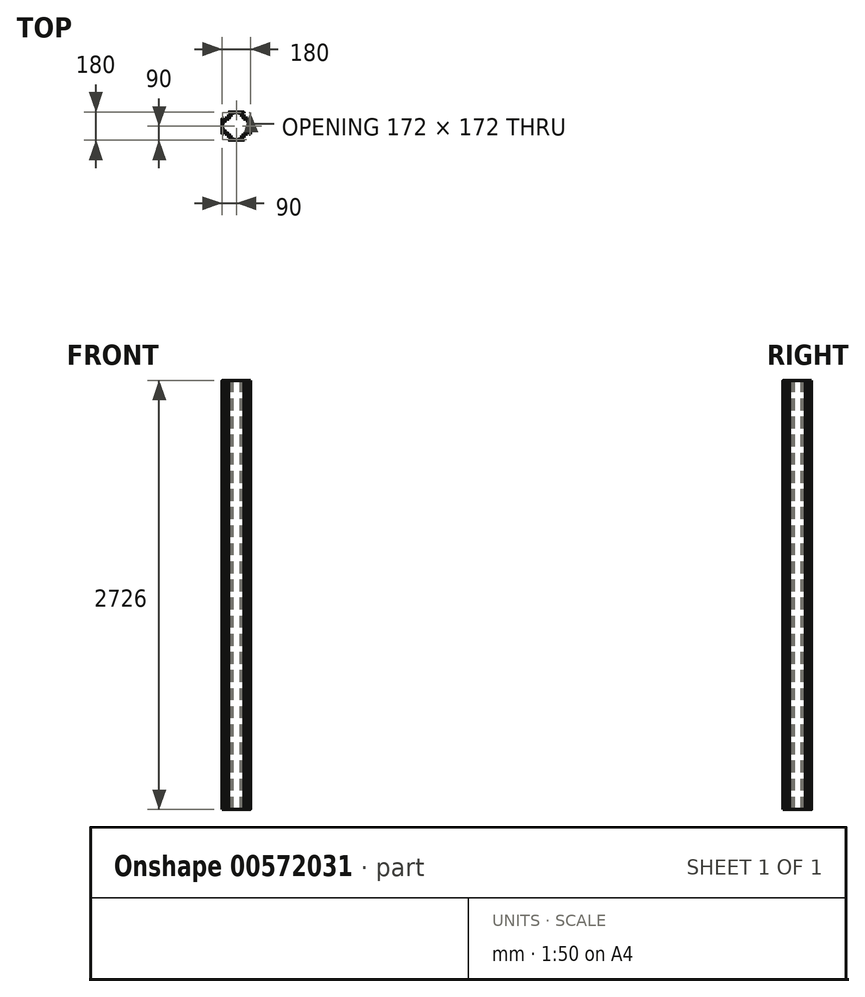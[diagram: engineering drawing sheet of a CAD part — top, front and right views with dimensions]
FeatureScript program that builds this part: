
annotation { "Feature Type Name" : "Feature", "Feature Type Description" : "" }
export const myFeature = defineFeature(function(context is Context, id is Id, definition is map)
    precondition{}
    {
        {
            var Q0;
            Q0=qCreatedBy(makeId("Top.planeOp"),FACE);
            var sketch = newSketch(context, id + "F0", { "sketchPlane" : qUnion([Q0])});
            skLineSegment(sketch, "E0", {"start": v(-58.4, 0) * mm, "end": v(68.52, 0) * mm, "construction": true});
            skLineSegment(sketch, "E1", {"start": v(0, 55.81) * mm, "end": v(0, -52.18) * mm, "construction": true});
            skLineSegment(sketch, "E2.bottom", {"start": v(-50, 90) * mm, "end": v(50, 90) * mm});
            skLineSegment(sketch, "E2.top", {"start": v(-50, -90) * mm, "end": v(50, -90) * mm});
            skLineSegment(sketch, "E2.left", {"start": v(-90, 50) * mm, "end": v(-90, -50) * mm});
            skLineSegment(sketch, "E2.right", {"start": v(90, 50) * mm, "end": v(90, -50) * mm});
            skLineSegment(sketch, "E3", {"start": v(-90, 50) * mm, "end": v(-82, 50) * mm});
            skLineSegment(sketch, "E4", {"start": v(-50, 50) * mm, "end": v(-50, 72) * mm});
            skLineSegment(sketch, "E5.MirrorCS", {"start": v(90, 50) * mm, "end": v(82, 50) * mm});
            skLineSegment(sketch, "E6.MirrorCS", {"start": v(50, 50) * mm, "end": v(50, 72) * mm});
            skLineSegment(sketch, "E7.MirrorCS", {"start": v(50, -50) * mm, "end": v(50, -72) * mm});
            skLineSegment(sketch, "E8.MirrorCS", {"start": v(90, -50) * mm, "end": v(82, -50) * mm});
            skLineSegment(sketch, "E9.MirrorCS", {"start": v(-50, -50) * mm, "end": v(-50, -72) * mm});
            skLineSegment(sketch, "E10.MirrorCS", {"start": v(-90, -50) * mm, "end": v(-82, -50) * mm});
            skLineSegment(sketch, "E11", {"start": v(-82, -50) * mm, "end": v(-82, -46) * mm});
            skLineSegment(sketch, "E12", {"start": v(-82, -46) * mm, "end": v(-86, -46) * mm});
            skLineSegment(sketch, "E13", {"start": v(-86, -46) * mm, "end": v(-86, -38) * mm});
            skLineSegment(sketch, "E14", {"start": v(-86, -38) * mm, "end": v(-68, -38) * mm});
            skLineSegment(sketch, "E15", {"start": v(-68, -38) * mm, "end": v(-68, -46) * mm});
            skLineSegment(sketch, "E16", {"start": v(-68, -46) * mm, "end": v(-72, -46) * mm});
            skLineSegment(sketch, "E17", {"start": v(-72, -46) * mm, "end": v(-72, -50) * mm});
            skLineSegment(sketch, "E18.MirrorCS", {"start": v(-68, 46) * mm, "end": v(-72, 46) * mm});
            skLineSegment(sketch, "E19.MirrorCS", {"start": v(-86, 38) * mm, "end": v(-68, 38) * mm});
            skLineSegment(sketch, "E20.MirrorCS", {"start": v(-82, 50) * mm, "end": v(-82, 46) * mm});
            skLineSegment(sketch, "E21.MirrorCS", {"start": v(-86, 46) * mm, "end": v(-86, 38) * mm});
            skLineSegment(sketch, "E22.MirrorCS", {"start": v(-82, 46) * mm, "end": v(-86, 46) * mm});
            skLineSegment(sketch, "E23.MirrorCS", {"start": v(-68, 38) * mm, "end": v(-68, 46) * mm});
            skLineSegment(sketch, "E24.MirrorCS", {"start": v(-72, 46) * mm, "end": v(-72, 50) * mm});
            skLineSegment(sketch, "E25.MirrorCS", {"start": v(68, -38) * mm, "end": v(68, -46) * mm});
            skLineSegment(sketch, "E26.MirrorCS", {"start": v(86, 38) * mm, "end": v(68, 38) * mm});
            skLineSegment(sketch, "E27.MirrorCS", {"start": v(82, 46) * mm, "end": v(86, 46) * mm});
            skLineSegment(sketch, "E28.MirrorCS", {"start": v(86, -38) * mm, "end": v(68, -38) * mm});
            skLineSegment(sketch, "E29.MirrorCS", {"start": v(68, 46) * mm, "end": v(72, 46) * mm});
            skLineSegment(sketch, "E30.MirrorCS", {"start": v(86, 46) * mm, "end": v(86, 38) * mm});
            skLineSegment(sketch, "E31.MirrorCS", {"start": v(86, -46) * mm, "end": v(86, -38) * mm});
            skLineSegment(sketch, "E32.MirrorCS", {"start": v(72, -46) * mm, "end": v(72, -50) * mm});
            skLineSegment(sketch, "E33.MirrorCS", {"start": v(82, 50) * mm, "end": v(82, 46) * mm});
            skLineSegment(sketch, "E34.MirrorCS", {"start": v(72, 46) * mm, "end": v(72, 50) * mm});
            skLineSegment(sketch, "E35.MirrorCS", {"start": v(68, 38) * mm, "end": v(68, 46) * mm});
            skLineSegment(sketch, "E36.MirrorCS", {"start": v(82, -50) * mm, "end": v(82, -46) * mm});
            skLineSegment(sketch, "E37.MirrorCS", {"start": v(68, -46) * mm, "end": v(72, -46) * mm});
            skLineSegment(sketch, "E38.MirrorCS", {"start": v(82, -46) * mm, "end": v(86, -46) * mm});
            skLineSegment(sketch, "E39", {"start": v(-50, 50) * mm, "end": v(0, 0) * mm, "construction": true});
            skLineSegment(sketch, "E40.MirrorCS", {"start": v(-38, 68) * mm, "end": v(-46, 68) * mm});
            skLineSegment(sketch, "E41.MirrorCS", {"start": v(-46, 68) * mm, "end": v(-46, 72) * mm});
            skLineSegment(sketch, "E42.MirrorCS", {"start": v(-46, 72) * mm, "end": v(-50, 72) * mm});
            skLineSegment(sketch, "E43.MirrorCS", {"start": v(-38, 86) * mm, "end": v(-38, 68) * mm});
            skLineSegment(sketch, "E44.MirrorCS", {"start": v(-46, 86) * mm, "end": v(-38, 86) * mm});
            skLineSegment(sketch, "E45.MirrorCS", {"start": v(-50, 82) * mm, "end": v(-46, 82) * mm});
            skLineSegment(sketch, "E46.MirrorCS", {"start": v(-46, 82) * mm, "end": v(-46, 86) * mm});
            skLineSegment(sketch, "E47.MirrorCS", {"start": v(46, 82) * mm, "end": v(46, 86) * mm});
            skLineSegment(sketch, "E48.MirrorCS", {"start": v(38, 86) * mm, "end": v(38, 68) * mm});
            skLineSegment(sketch, "E49.MirrorCS", {"start": v(46, 68) * mm, "end": v(46, 72) * mm});
            skLineSegment(sketch, "E50.MirrorCS", {"start": v(50, 82) * mm, "end": v(46, 82) * mm});
            skLineSegment(sketch, "E51.MirrorCS", {"start": v(46, 86) * mm, "end": v(38, 86) * mm});
            skLineSegment(sketch, "E52.MirrorCS", {"start": v(38, 68) * mm, "end": v(46, 68) * mm});
            skLineSegment(sketch, "E53.MirrorCS", {"start": v(46, 72) * mm, "end": v(50, 72) * mm});
            skLineSegment(sketch, "E54.MirrorCS", {"start": v(-46, -86) * mm, "end": v(-38, -86) * mm});
            skLineSegment(sketch, "E55.MirrorCS", {"start": v(50, -82) * mm, "end": v(46, -82) * mm});
            skLineSegment(sketch, "E56.MirrorCS", {"start": v(-38, -86) * mm, "end": v(-38, -68) * mm});
            skLineSegment(sketch, "E57.MirrorCS", {"start": v(-46, -82) * mm, "end": v(-46, -86) * mm});
            skLineSegment(sketch, "E58.MirrorCS", {"start": v(-38, -68) * mm, "end": v(-46, -68) * mm});
            skLineSegment(sketch, "E59.MirrorCS", {"start": v(38, -86) * mm, "end": v(38, -68) * mm});
            skLineSegment(sketch, "E60.MirrorCS", {"start": v(-50, -82) * mm, "end": v(-46, -82) * mm});
            skLineSegment(sketch, "E61.MirrorCS", {"start": v(-46, -72) * mm, "end": v(-50, -72) * mm});
            skLineSegment(sketch, "E62.MirrorCS", {"start": v(-46, -68) * mm, "end": v(-46, -72) * mm});
            skLineSegment(sketch, "E63.MirrorCS", {"start": v(46, -72) * mm, "end": v(50, -72) * mm});
            skLineSegment(sketch, "E64.MirrorCS", {"start": v(38, -68) * mm, "end": v(46, -68) * mm});
            skLineSegment(sketch, "E65.MirrorCS", {"start": v(46, -68) * mm, "end": v(46, -72) * mm});
            skLineSegment(sketch, "E66.MirrorCS", {"start": v(46, -82) * mm, "end": v(46, -86) * mm});
            skLineSegment(sketch, "E67.MirrorCS", {"start": v(46, -86) * mm, "end": v(38, -86) * mm});
            skLineSegment(sketch, "E68.trimOffspring", {"start": v(-72, 50) * mm, "end": v(-50, 50) * mm});
            skLineSegment(sketch, "E69.trimOffspring", {"start": v(-50, 82) * mm, "end": v(-50, 90) * mm});
            skLineSegment(sketch, "E70.trimOffspring", {"start": v(50, 82) * mm, "end": v(50, 90) * mm});
            skLineSegment(sketch, "E71.trimOffspring", {"start": v(72, 50) * mm, "end": v(50, 50) * mm});
            skLineSegment(sketch, "E72.trimOffspring", {"start": v(72, -50) * mm, "end": v(50, -50) * mm});
            skLineSegment(sketch, "E73.trimOffspring", {"start": v(50, -82) * mm, "end": v(50, -90) * mm});
            skLineSegment(sketch, "E74.trimOffspring", {"start": v(-50, -82) * mm, "end": v(-50, -90) * mm});
            skLineSegment(sketch, "E75.trimOffspring", {"start": v(-72, -50) * mm, "end": v(-50, -50) * mm});
            skSolve(sketch);
        }
        {
            var Q0;
            Q0=qSketchRegion(id+"F0",true);
            extrude(context, id + "F1", {"entities" : qUnion([Q0]), "depth" : 2726 * mm, "offsetDistance" : 25 * mm});
        }
        {
            var Q0;
            Q0=makeQuery(id+"F1.opExtrude","CAP_FACE",FACE,{"disambiguationData":[OSD([sQuery(id+"F0.wireOp",EDGE,"E2.bottom"),sQuery(id+"F0.wireOp",EDGE,"E2.top"),sQuery(id+"F0.wireOp",EDGE,"E2.left"),sQuery(id+"F0.wireOp",EDGE,"E2.right"),sQuery(id+"F0.wireOp",EDGE,"E3"),sQuery(id+"F0.wireOp",EDGE,"E4"),sQuery(id+"F0.wireOp",EDGE,"E5.MirrorCS"),sQuery(id+"F0.wireOp",EDGE,"E6.MirrorCS"),sQuery(id+"F0.wireOp",EDGE,"E7.MirrorCS"),sQuery(id+"F0.wireOp",EDGE,"E8.MirrorCS"),sQuery(id+"F0.wireOp",EDGE,"E9.MirrorCS"),sQuery(id+"F0.wireOp",EDGE,"E10.MirrorCS")])],"isStart":false});
            var Q1;
            Q1=makeQuery(id+"F1.opExtrude","CAP_FACE",FACE,{"disambiguationData":[OSD([sQuery(id+"F0.wireOp",EDGE,"E2.bottom"),sQuery(id+"F0.wireOp",EDGE,"E2.top"),sQuery(id+"F0.wireOp",EDGE,"E2.left"),sQuery(id+"F0.wireOp",EDGE,"E2.right"),sQuery(id+"F0.wireOp",EDGE,"E3"),sQuery(id+"F0.wireOp",EDGE,"E4"),sQuery(id+"F0.wireOp",EDGE,"E5.MirrorCS"),sQuery(id+"F0.wireOp",EDGE,"E6.MirrorCS"),sQuery(id+"F0.wireOp",EDGE,"E7.MirrorCS"),sQuery(id+"F0.wireOp",EDGE,"E8.MirrorCS"),sQuery(id+"F0.wireOp",EDGE,"E9.MirrorCS"),sQuery(id+"F0.wireOp",EDGE,"E10.MirrorCS")])],"isStart":true});
            shell(context, id + "F2", {"entities" : qUnion([Q0, Q1]), "thickness" : 4 * mm});
        }
        {
            var Q0;
            Q0=makeQuery(id+"F1.opExtrude","SWEPT_EDGE",EDGE,{"disambiguationData":[OSD([sQuery(id+"F0.wireOp",EDGE,"E2.top"),sQuery(id+"F0.wireOp",EDGE,"E74.trimOffspring")])]});
            var Q1;
            Q1=makeQuery(id+"F1.opExtrude","SWEPT_EDGE",EDGE,{"disambiguationData":[OSD([sQuery(id+"F0.wireOp",EDGE,"E2.left"),sQuery(id+"F0.wireOp",EDGE,"E10.MirrorCS")])]});
            var Q2;
            Q2=makeQuery(id+"F1.opExtrude","SWEPT_EDGE",EDGE,{"disambiguationData":[OSD([sQuery(id+"F0.wireOp",EDGE,"E2.top"),sQuery(id+"F0.wireOp",EDGE,"E73.trimOffspring")])]});
            var Q3;
            Q3=makeQuery(id+"F1.opExtrude","SWEPT_EDGE",EDGE,{"disambiguationData":[OSD([sQuery(id+"F0.wireOp",EDGE,"E2.right"),sQuery(id+"F0.wireOp",EDGE,"E8.MirrorCS")])]});
            var Q4;
            Q4=makeQuery(id+"F1.opExtrude","SWEPT_EDGE",EDGE,{"disambiguationData":[OSD([sQuery(id+"F0.wireOp",EDGE,"E2.right"),sQuery(id+"F0.wireOp",EDGE,"E5.MirrorCS")])]});
            var Q5;
            Q5=makeQuery(id+"F1.opExtrude","SWEPT_EDGE",EDGE,{"disambiguationData":[OSD([sQuery(id+"F0.wireOp",EDGE,"E2.bottom"),sQuery(id+"F0.wireOp",EDGE,"E70.trimOffspring")])]});
            var Q6;
            Q6=makeQuery(id+"F1.opExtrude","SWEPT_EDGE",EDGE,{"disambiguationData":[OSD([sQuery(id+"F0.wireOp",EDGE,"E2.bottom"),sQuery(id+"F0.wireOp",EDGE,"E69.trimOffspring")])]});
            var Q7;
            Q7=makeQuery(id+"F1.opExtrude","SWEPT_EDGE",EDGE,{"disambiguationData":[OSD([sQuery(id+"F0.wireOp",EDGE,"E2.left"),sQuery(id+"F0.wireOp",EDGE,"E3")])]});
            fillet(context, id + "F3", {"entities" : qUnion([Q0, Q1, Q2, Q3, Q4, Q5, Q6, Q7]), "radius" : 3 * mm, "tangentPropagation" : true, "allowEdgeOverflow" : false});
        }
        {
            var Q0;
            Q0=makeQuery(id+"F1.opExtrude","CAP_FACE",FACE,{"disambiguationData":[OSD([sQuery(id+"F0.wireOp",EDGE,"E2.bottom"),sQuery(id+"F0.wireOp",EDGE,"E2.top"),sQuery(id+"F0.wireOp",EDGE,"E2.left"),sQuery(id+"F0.wireOp",EDGE,"E2.right"),sQuery(id+"F0.wireOp",EDGE,"E3"),sQuery(id+"F0.wireOp",EDGE,"E4"),sQuery(id+"F0.wireOp",EDGE,"E5.MirrorCS"),sQuery(id+"F0.wireOp",EDGE,"E6.MirrorCS"),sQuery(id+"F0.wireOp",EDGE,"E7.MirrorCS"),sQuery(id+"F0.wireOp",EDGE,"E8.MirrorCS"),sQuery(id+"F0.wireOp",EDGE,"E9.MirrorCS"),sQuery(id+"F0.wireOp",EDGE,"E10.MirrorCS"),sQuery(id+"F0.wireOp",EDGE,"E11"),sQuery(id+"F0.wireOp",EDGE,"E12"),sQuery(id+"F0.wireOp",EDGE,"E13"),sQuery(id+"F0.wireOp",EDGE,"E14"),sQuery(id+"F0.wireOp",EDGE,"E15"),sQuery(id+"F0.wireOp",EDGE,"E16"),sQuery(id+"F0.wireOp",EDGE,"E17"),sQuery(id+"F0.wireOp",EDGE,"E18.MirrorCS"),sQuery(id+"F0.wireOp",EDGE,"E19.MirrorCS"),sQuery(id+"F0.wireOp",EDGE,"E20.MirrorCS"),sQuery(id+"F0.wireOp",EDGE,"E21.MirrorCS"),sQuery(id+"F0.wireOp",EDGE,"E22.MirrorCS"),sQuery(id+"F0.wireOp",EDGE,"E23.MirrorCS"),sQuery(id+"F0.wireOp",EDGE,"E24.MirrorCS"),sQuery(id+"F0.wireOp",EDGE,"E25.MirrorCS"),sQuery(id+"F0.wireOp",EDGE,"E26.MirrorCS"),sQuery(id+"F0.wireOp",EDGE,"E27.MirrorCS"),sQuery(id+"F0.wireOp",EDGE,"E28.MirrorCS"),sQuery(id+"F0.wireOp",EDGE,"E29.MirrorCS"),sQuery(id+"F0.wireOp",EDGE,"E30.MirrorCS"),sQuery(id+"F0.wireOp",EDGE,"E31.MirrorCS"),sQuery(id+"F0.wireOp",EDGE,"E32.MirrorCS"),sQuery(id+"F0.wireOp",EDGE,"E33.MirrorCS"),sQuery(id+"F0.wireOp",EDGE,"E34.MirrorCS"),sQuery(id+"F0.wireOp",EDGE,"E35.MirrorCS"),sQuery(id+"F0.wireOp",EDGE,"E36.MirrorCS"),sQuery(id+"F0.wireOp",EDGE,"E37.MirrorCS"),sQuery(id+"F0.wireOp",EDGE,"E38.MirrorCS"),sQuery(id+"F0.wireOp",EDGE,"E40.MirrorCS"),sQuery(id+"F0.wireOp",EDGE,"E41.MirrorCS"),sQuery(id+"F0.wireOp",EDGE,"E42.MirrorCS"),sQuery(id+"F0.wireOp",EDGE,"E43.MirrorCS"),sQuery(id+"F0.wireOp",EDGE,"E44.MirrorCS"),sQuery(id+"F0.wireOp",EDGE,"E45.MirrorCS"),sQuery(id+"F0.wireOp",EDGE,"E46.MirrorCS"),sQuery(id+"F0.wireOp",EDGE,"E47.MirrorCS"),sQuery(id+"F0.wireOp",EDGE,"E48.MirrorCS"),sQuery(id+"F0.wireOp",EDGE,"E49.MirrorCS"),sQuery(id+"F0.wireOp",EDGE,"E50.MirrorCS"),sQuery(id+"F0.wireOp",EDGE,"E51.MirrorCS"),sQuery(id+"F0.wireOp",EDGE,"E52.MirrorCS"),sQuery(id+"F0.wireOp",EDGE,"E53.MirrorCS"),sQuery(id+"F0.wireOp",EDGE,"E54.MirrorCS"),sQuery(id+"F0.wireOp",EDGE,"E55.MirrorCS"),sQuery(id+"F0.wireOp",EDGE,"E56.MirrorCS"),sQuery(id+"F0.wireOp",EDGE,"E57.MirrorCS"),sQuery(id+"F0.wireOp",EDGE,"E58.MirrorCS"),sQuery(id+"F0.wireOp",EDGE,"E59.MirrorCS"),sQuery(id+"F0.wireOp",EDGE,"E60.MirrorCS"),sQuery(id+"F0.wireOp",EDGE,"E61.MirrorCS"),sQuery(id+"F0.wireOp",EDGE,"E62.MirrorCS"),sQuery(id+"F0.wireOp",EDGE,"E63.MirrorCS"),sQuery(id+"F0.wireOp",EDGE,"E64.MirrorCS"),sQuery(id+"F0.wireOp",EDGE,"E65.MirrorCS"),sQuery(id+"F0.wireOp",EDGE,"E66.MirrorCS"),sQuery(id+"F0.wireOp",EDGE,"E67.MirrorCS"),sQuery(id+"F0.wireOp",EDGE,"E68.trimOffspring"),sQuery(id+"F0.wireOp",EDGE,"E69.trimOffspring"),sQuery(id+"F0.wireOp",EDGE,"E70.trimOffspring"),sQuery(id+"F0.wireOp",EDGE,"E71.trimOffspring"),sQuery(id+"F0.wireOp",EDGE,"E72.trimOffspring"),sQuery(id+"F0.wireOp",EDGE,"E73.trimOffspring"),sQuery(id+"F0.wireOp",EDGE,"E74.trimOffspring"),sQuery(id+"F0.wireOp",EDGE,"E75.trimOffspring")])],"isStart":true});
            var sketch = newSketch(context, id + "F4", { "sketchPlane" : qUnion([Q0])});
            skLineSegment(sketch, "E76.bottom", {"start": v(-64, 38) * mm, "end": v(-61, 38) * mm});
            skLineSegment(sketch, "E76.top", {"start": v(-64, 34) * mm, "end": v(-61, 34) * mm});
            skLineSegment(sketch, "E76.left", {"start": v(-64, 38) * mm, "end": v(-64, 34) * mm});
            skLineSegment(sketch, "E76.right", {"start": v(-61, 38) * mm, "end": v(-61, 34) * mm});
            skLineSegment(sketch, "E77", {"start": v(-74, 34) * mm, "end": v(-74, 23) * mm});
            skLineSegment(sketch, "E78", {"start": v(-74, 23) * mm, "end": v(-78, 23) * mm});
            skLineSegment(sketch, "E79", {"start": v(-78, 23) * mm, "end": v(-78, 34) * mm});
            skLineSegment(sketch, "E80", {"start": v(-78, 34) * mm, "end": v(-74, 34) * mm});
            skLineSegment(sketch, "E81", {"start": v(0, 86) * mm, "end": v(0, 0) * mm, "construction": true});
            skLineSegment(sketch, "E82", {"start": v(0, 0) * mm, "end": v(-86, 0) * mm, "construction": true});
            skLineSegment(sketch, "E83.MirrorCS", {"start": v(64, 38) * mm, "end": v(64, 34) * mm});
            skLineSegment(sketch, "E84.MirrorCS", {"start": v(61, 38) * mm, "end": v(61, 34) * mm});
            skLineSegment(sketch, "E85.MirrorCS", {"start": v(78, 34) * mm, "end": v(74, 34) * mm});
            skLineSegment(sketch, "E86.MirrorCS", {"start": v(74, 23) * mm, "end": v(78, 23) * mm});
            skLineSegment(sketch, "E87.MirrorCS", {"start": v(64, 38) * mm, "end": v(61, 38) * mm});
            skLineSegment(sketch, "E88.MirrorCS", {"start": v(64, 34) * mm, "end": v(61, 34) * mm});
            skLineSegment(sketch, "E89.MirrorCS", {"start": v(78, 23) * mm, "end": v(78, 34) * mm});
            skLineSegment(sketch, "E90.MirrorCS", {"start": v(74, 34) * mm, "end": v(74, 23) * mm});
            skLineSegment(sketch, "E91.MirrorCS", {"start": v(0, 0) * mm, "end": v(86, 0) * mm, "construction": true});
            skLineSegment(sketch, "E92.MirrorCS", {"start": v(74, -34) * mm, "end": v(74, -23) * mm});
            skLineSegment(sketch, "E93.MirrorCS", {"start": v(74, -23) * mm, "end": v(78, -23) * mm});
            skLineSegment(sketch, "E94.MirrorCS", {"start": v(64, -38) * mm, "end": v(61, -38) * mm});
            skLineSegment(sketch, "E95.MirrorCS", {"start": v(64, -34) * mm, "end": v(61, -34) * mm});
            skLineSegment(sketch, "E96.MirrorCS", {"start": v(-64, -38) * mm, "end": v(-61, -38) * mm});
            skLineSegment(sketch, "E97.MirrorCS", {"start": v(-64, -34) * mm, "end": v(-61, -34) * mm});
            skLineSegment(sketch, "E98.MirrorCS", {"start": v(-64, -38) * mm, "end": v(-64, -34) * mm});
            skLineSegment(sketch, "E99.MirrorCS", {"start": v(-61, -38) * mm, "end": v(-61, -34) * mm});
            skLineSegment(sketch, "E100.MirrorCS", {"start": v(-74, -34) * mm, "end": v(-74, -23) * mm});
            skLineSegment(sketch, "E101.MirrorCS", {"start": v(-74, -23) * mm, "end": v(-78, -23) * mm});
            skLineSegment(sketch, "E102.MirrorCS", {"start": v(78, -34) * mm, "end": v(74, -34) * mm});
            skLineSegment(sketch, "E103.MirrorCS", {"start": v(61, -38) * mm, "end": v(61, -34) * mm});
            skLineSegment(sketch, "E104.MirrorCS", {"start": v(78, -23) * mm, "end": v(78, -34) * mm});
            skLineSegment(sketch, "E105.MirrorCS", {"start": v(-78, -34) * mm, "end": v(-74, -34) * mm});
            skLineSegment(sketch, "E106.MirrorCS", {"start": v(-78, -23) * mm, "end": v(-78, -34) * mm});
            skLineSegment(sketch, "E107.MirrorCS", {"start": v(64, -38) * mm, "end": v(64, -34) * mm});
            skLineSegment(sketch, "E108", {"start": v(-46, 46) * mm, "end": v(0, 0) * mm, "construction": true});
            skLineSegment(sketch, "E109.MirrorCS", {"start": v(-34, 78) * mm, "end": v(-34, 74) * mm});
            skLineSegment(sketch, "E110.MirrorCS", {"start": v(-23, 78) * mm, "end": v(-34, 78) * mm});
            skLineSegment(sketch, "E111.MirrorCS", {"start": v(-23, 74) * mm, "end": v(-23, 78) * mm});
            skLineSegment(sketch, "E112.MirrorCS", {"start": v(-34, 74) * mm, "end": v(-23, 74) * mm});
            skLineSegment(sketch, "E113.MirrorCS", {"start": v(-38, 61) * mm, "end": v(-34, 61) * mm});
            skLineSegment(sketch, "E114.MirrorCS", {"start": v(-38, 64) * mm, "end": v(-34, 64) * mm});
            skLineSegment(sketch, "E115.MirrorCS", {"start": v(-38, 64) * mm, "end": v(-38, 61) * mm});
            skLineSegment(sketch, "E116.MirrorCS", {"start": v(-34, 64) * mm, "end": v(-34, 61) * mm});
            skLineSegment(sketch, "E117.MirrorCS", {"start": v(34, 78) * mm, "end": v(34, 74) * mm});
            skLineSegment(sketch, "E118.MirrorCS", {"start": v(34, 64) * mm, "end": v(34, 61) * mm});
            skLineSegment(sketch, "E119.MirrorCS", {"start": v(23, 78) * mm, "end": v(34, 78) * mm});
            skLineSegment(sketch, "E120.MirrorCS", {"start": v(23, 74) * mm, "end": v(23, 78) * mm});
            skLineSegment(sketch, "E121.MirrorCS", {"start": v(34, 74) * mm, "end": v(23, 74) * mm});
            skLineSegment(sketch, "E122.MirrorCS", {"start": v(38, 61) * mm, "end": v(34, 61) * mm});
            skLineSegment(sketch, "E123.MirrorCS", {"start": v(38, 64) * mm, "end": v(38, 61) * mm});
            skLineSegment(sketch, "E124.MirrorCS", {"start": v(38, 64) * mm, "end": v(34, 64) * mm});
            skLineSegment(sketch, "E125.MirrorCS", {"start": v(-34, -78) * mm, "end": v(-34, -74) * mm});
            skLineSegment(sketch, "E126.MirrorCS", {"start": v(34, -64) * mm, "end": v(34, -61) * mm});
            skLineSegment(sketch, "E127.MirrorCS", {"start": v(-34, -64) * mm, "end": v(-34, -61) * mm});
            skLineSegment(sketch, "E128.MirrorCS", {"start": v(34, -78) * mm, "end": v(34, -74) * mm});
            skLineSegment(sketch, "E129.MirrorCS", {"start": v(-23, -78) * mm, "end": v(-34, -78) * mm});
            skLineSegment(sketch, "E130.MirrorCS", {"start": v(23, -78) * mm, "end": v(34, -78) * mm});
            skLineSegment(sketch, "E131.MirrorCS", {"start": v(23, -74) * mm, "end": v(23, -78) * mm});
            skLineSegment(sketch, "E132.MirrorCS", {"start": v(-23, -74) * mm, "end": v(-23, -78) * mm});
            skLineSegment(sketch, "E133.MirrorCS", {"start": v(38, -64) * mm, "end": v(34, -64) * mm});
            skLineSegment(sketch, "E134.MirrorCS", {"start": v(38, -64) * mm, "end": v(38, -61) * mm});
            skLineSegment(sketch, "E135.MirrorCS", {"start": v(-38, -64) * mm, "end": v(-34, -64) * mm});
            skLineSegment(sketch, "E136.MirrorCS", {"start": v(34, -74) * mm, "end": v(23, -74) * mm});
            skLineSegment(sketch, "E137.MirrorCS", {"start": v(38, -61) * mm, "end": v(34, -61) * mm});
            skLineSegment(sketch, "E138.MirrorCS", {"start": v(-38, -61) * mm, "end": v(-34, -61) * mm});
            skLineSegment(sketch, "E139.MirrorCS", {"start": v(-34, -74) * mm, "end": v(-23, -74) * mm});
            skLineSegment(sketch, "E140.MirrorCS", {"start": v(-38, -64) * mm, "end": v(-38, -61) * mm});
            skSolve(sketch);
        }
        {
            var Q0;
            Q0=qSketchRegion(id+"F4",true);
            var Q1;
            Q1=makeQuery(id+"F1.opExtrude","CAP_FACE",FACE,{"disambiguationData":[OSD([sQuery(id+"F0.wireOp",EDGE,"E2.bottom"),sQuery(id+"F0.wireOp",EDGE,"E2.top"),sQuery(id+"F0.wireOp",EDGE,"E2.left"),sQuery(id+"F0.wireOp",EDGE,"E2.right"),sQuery(id+"F0.wireOp",EDGE,"E3"),sQuery(id+"F0.wireOp",EDGE,"E4"),sQuery(id+"F0.wireOp",EDGE,"E5.MirrorCS"),sQuery(id+"F0.wireOp",EDGE,"E6.MirrorCS"),sQuery(id+"F0.wireOp",EDGE,"E7.MirrorCS"),sQuery(id+"F0.wireOp",EDGE,"E8.MirrorCS"),sQuery(id+"F0.wireOp",EDGE,"E9.MirrorCS"),sQuery(id+"F0.wireOp",EDGE,"E10.MirrorCS"),sQuery(id+"F0.wireOp",EDGE,"E11"),sQuery(id+"F0.wireOp",EDGE,"E12"),sQuery(id+"F0.wireOp",EDGE,"E13"),sQuery(id+"F0.wireOp",EDGE,"E14"),sQuery(id+"F0.wireOp",EDGE,"E15"),sQuery(id+"F0.wireOp",EDGE,"E16"),sQuery(id+"F0.wireOp",EDGE,"E17"),sQuery(id+"F0.wireOp",EDGE,"E18.MirrorCS"),sQuery(id+"F0.wireOp",EDGE,"E19.MirrorCS"),sQuery(id+"F0.wireOp",EDGE,"E20.MirrorCS"),sQuery(id+"F0.wireOp",EDGE,"E21.MirrorCS"),sQuery(id+"F0.wireOp",EDGE,"E22.MirrorCS"),sQuery(id+"F0.wireOp",EDGE,"E23.MirrorCS"),sQuery(id+"F0.wireOp",EDGE,"E24.MirrorCS"),sQuery(id+"F0.wireOp",EDGE,"E25.MirrorCS"),sQuery(id+"F0.wireOp",EDGE,"E26.MirrorCS"),sQuery(id+"F0.wireOp",EDGE,"E27.MirrorCS"),sQuery(id+"F0.wireOp",EDGE,"E28.MirrorCS"),sQuery(id+"F0.wireOp",EDGE,"E29.MirrorCS"),sQuery(id+"F0.wireOp",EDGE,"E30.MirrorCS"),sQuery(id+"F0.wireOp",EDGE,"E31.MirrorCS"),sQuery(id+"F0.wireOp",EDGE,"E32.MirrorCS"),sQuery(id+"F0.wireOp",EDGE,"E33.MirrorCS"),sQuery(id+"F0.wireOp",EDGE,"E34.MirrorCS"),sQuery(id+"F0.wireOp",EDGE,"E35.MirrorCS"),sQuery(id+"F0.wireOp",EDGE,"E36.MirrorCS"),sQuery(id+"F0.wireOp",EDGE,"E37.MirrorCS"),sQuery(id+"F0.wireOp",EDGE,"E38.MirrorCS"),sQuery(id+"F0.wireOp",EDGE,"E40.MirrorCS"),sQuery(id+"F0.wireOp",EDGE,"E41.MirrorCS"),sQuery(id+"F0.wireOp",EDGE,"E42.MirrorCS"),sQuery(id+"F0.wireOp",EDGE,"E43.MirrorCS"),sQuery(id+"F0.wireOp",EDGE,"E44.MirrorCS"),sQuery(id+"F0.wireOp",EDGE,"E45.MirrorCS"),sQuery(id+"F0.wireOp",EDGE,"E46.MirrorCS"),sQuery(id+"F0.wireOp",EDGE,"E47.MirrorCS"),sQuery(id+"F0.wireOp",EDGE,"E48.MirrorCS"),sQuery(id+"F0.wireOp",EDGE,"E49.MirrorCS"),sQuery(id+"F0.wireOp",EDGE,"E50.MirrorCS"),sQuery(id+"F0.wireOp",EDGE,"E51.MirrorCS"),sQuery(id+"F0.wireOp",EDGE,"E52.MirrorCS"),sQuery(id+"F0.wireOp",EDGE,"E53.MirrorCS"),sQuery(id+"F0.wireOp",EDGE,"E54.MirrorCS"),sQuery(id+"F0.wireOp",EDGE,"E55.MirrorCS"),sQuery(id+"F0.wireOp",EDGE,"E56.MirrorCS"),sQuery(id+"F0.wireOp",EDGE,"E57.MirrorCS"),sQuery(id+"F0.wireOp",EDGE,"E58.MirrorCS"),sQuery(id+"F0.wireOp",EDGE,"E59.MirrorCS"),sQuery(id+"F0.wireOp",EDGE,"E60.MirrorCS"),sQuery(id+"F0.wireOp",EDGE,"E61.MirrorCS"),sQuery(id+"F0.wireOp",EDGE,"E62.MirrorCS"),sQuery(id+"F0.wireOp",EDGE,"E63.MirrorCS"),sQuery(id+"F0.wireOp",EDGE,"E64.MirrorCS"),sQuery(id+"F0.wireOp",EDGE,"E65.MirrorCS"),sQuery(id+"F0.wireOp",EDGE,"E66.MirrorCS"),sQuery(id+"F0.wireOp",EDGE,"E67.MirrorCS"),sQuery(id+"F0.wireOp",EDGE,"E68.trimOffspring"),sQuery(id+"F0.wireOp",EDGE,"E69.trimOffspring"),sQuery(id+"F0.wireOp",EDGE,"E70.trimOffspring"),sQuery(id+"F0.wireOp",EDGE,"E71.trimOffspring"),sQuery(id+"F0.wireOp",EDGE,"E72.trimOffspring"),sQuery(id+"F0.wireOp",EDGE,"E73.trimOffspring"),sQuery(id+"F0.wireOp",EDGE,"E74.trimOffspring"),sQuery(id+"F0.wireOp",EDGE,"E75.trimOffspring")])],"isStart":false});
            extrude(context, id + "F5", {"entities" : qUnion([Q0]), "operationType" : NewBodyOperationType.ADD, "endBound" : BoundingType.UP_TO_SURFACE, "oppositeDirection" : true, "endBoundEntityFace" : qUnion([Q1]), "depth" : 25 * mm});
        }
    });
